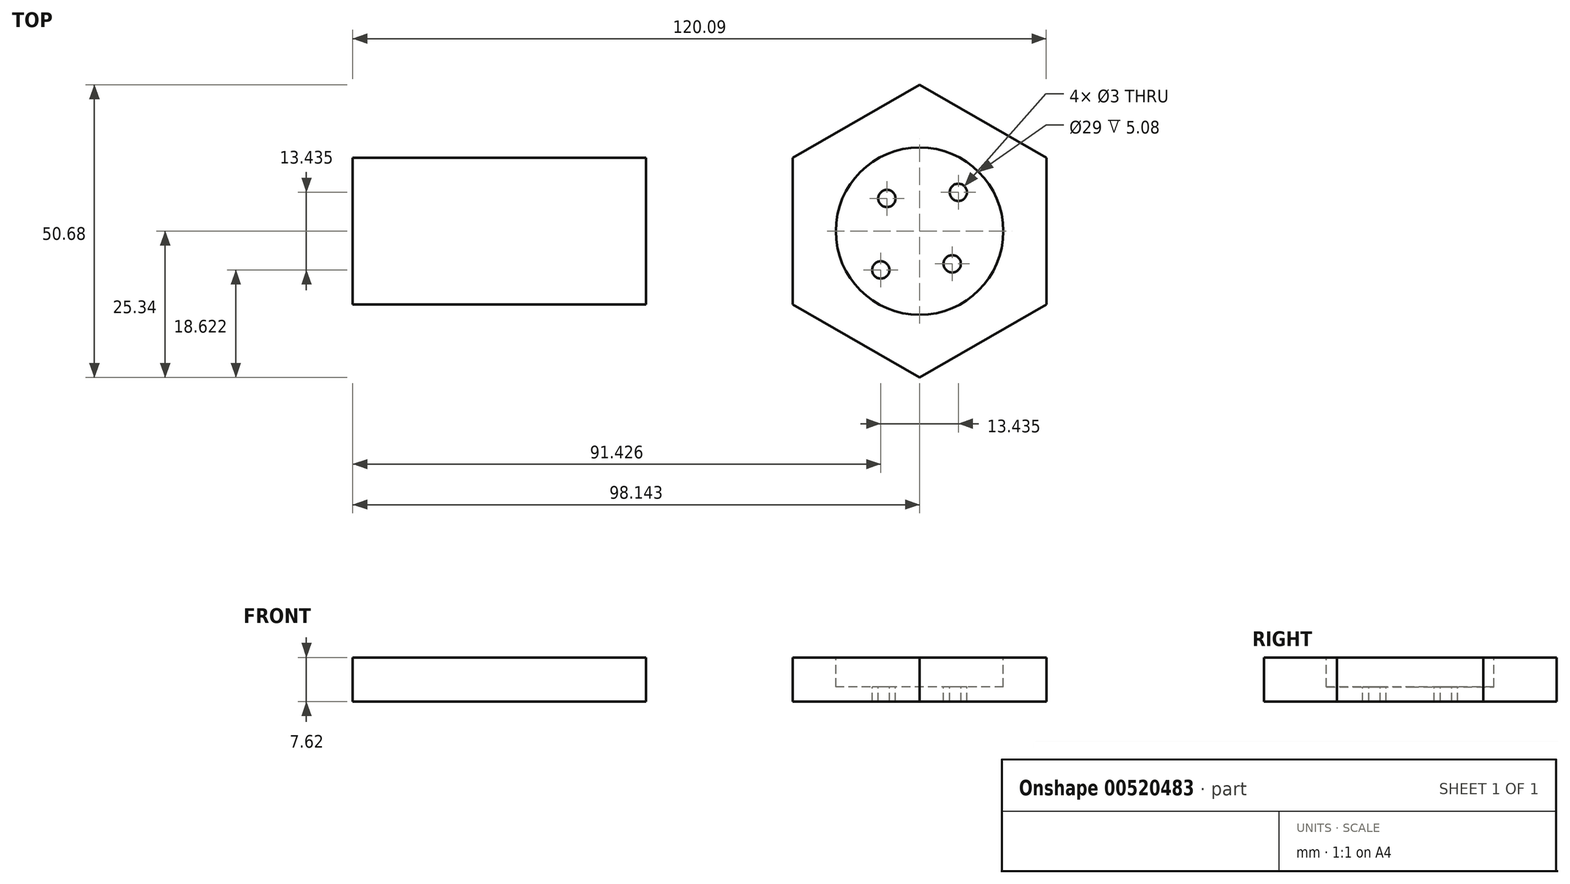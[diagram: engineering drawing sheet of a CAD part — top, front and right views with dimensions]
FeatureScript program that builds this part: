
annotation { "Feature Type Name" : "Feature", "Feature Type Description" : "" }
export const myFeature = defineFeature(function(context is Context, id is Id, definition is map)
    precondition{}
    {
        {
            var Q0;
            Q0=qCreatedBy(makeId("Top.planeOp"),FACE);
            var sketch = newSketch(context, id + "F0", { "sketchPlane" : qUnion([Q0])});
            skLineSegment(sketch, "E0.bottom", {"start": v(25.4, -12.7) * mm, "end": v(-25.4, -12.7) * mm});
            skLineSegment(sketch, "E0.top", {"start": v(25.4, 12.7) * mm, "end": v(-25.4, 12.7) * mm});
            skLineSegment(sketch, "E0.left", {"start": v(25.4, -12.7) * mm, "end": v(25.4, 12.7) * mm});
            skLineSegment(sketch, "E0.right", {"start": v(-25.4, -12.7) * mm, "end": v(-25.4, 12.7) * mm});
            skPoint(sketch, "E0.middle", {"position": v(0, 0) * mm});
            skSolve(sketch);
        }
        {
            var Q0;
            Q0=qCreatedBy(makeId("Top.planeOp"),FACE);
            var sketch = newSketch(context, id + "F1", { "sketchPlane" : qUnion([Q0])});
            skCircle(sketch, "E1.cCircle", {"center": v(72.74, 0) * mm, "radius": 21.95 * mm, "construction": true});
            skLineSegment(sketch, "E1.0", {"start": v(94.7, 12.67) * mm, "end": v(94.7, -12.67) * mm});
            skLineSegment(sketch, "E1.1", {"start": v(94.7, -12.67) * mm, "end": v(72.74, -25.34) * mm});
            skLineSegment(sketch, "E1.2", {"start": v(72.74, -25.34) * mm, "end": v(50.8, -12.67) * mm});
            skLineSegment(sketch, "E1.3", {"start": v(50.8, -12.67) * mm, "end": v(50.8, 12.67) * mm});
            skLineSegment(sketch, "E1.4", {"start": v(50.8, 12.67) * mm, "end": v(72.74, 25.34) * mm});
            skLineSegment(sketch, "E1.5", {"start": v(72.74, 25.34) * mm, "end": v(94.7, 12.67) * mm});
            skPoint(sketch, "E1.0.midPoint", {"position": v(94.7, 0) * mm});
            skSolve(sketch);
        }
        {
            var Q0;
            Q0=makeQuery(id+"F1.imprint","IMPRINT",FACE,{"disambiguationData":[TD([[makeQuery(id+"F1.imprint","IMPRINT",EDGE,{"derivedFrom":sQuery(id+"F1.wireOp",EDGE,"E1.0")}),-1.0]])]});
            extrude(context, id + "F2", {"entities" : qUnion([Q0]), "depth" : 7.62 * mm, "offsetDistance" : 25.4 * mm});
        }
        {
            var Q0;
            Q0=makeQuery(id+"F2.opExtrude","CAP_FACE",FACE,{"disambiguationData":[OSD([sQuery(id+"F1.wireOp",EDGE,"E1.0"),sQuery(id+"F1.wireOp",EDGE,"E1.1"),sQuery(id+"F1.wireOp",EDGE,"E1.2"),sQuery(id+"F1.wireOp",EDGE,"E1.3"),sQuery(id+"F1.wireOp",EDGE,"E1.4"),sQuery(id+"F1.wireOp",EDGE,"E1.5")])],"isStart":false});
            var sketch = newSketch(context, id + "F3", { "sketchPlane" : qUnion([Q0])});
            skCircle(sketch, "E2", {"center": v(72.74, 0) * mm, "radius": 14.5 * mm});
            skSolve(sketch);
        }
        {
            var Q0;
            Q0 = qSketchRegion(id + "F3", true);
            extrude(context, id + "F4", {"entities" : qUnion([Q0]), "operationType" : NewBodyOperationType.REMOVE, "oppositeDirection" : true, "depth" : 5.08 * mm, "offsetDistance" : 25.4 * mm});
        }
        {
            var Q0;
            Q0=makeQuery(id+"F4.boolean.opBoolean","COPY",FACE,{"derivedFrom":makeQuery(id+"F4.opExtrude","CAP_FACE",FACE,{"disambiguationData":[OSD([sQuery(id+"F3.wireOp",EDGE,"E2")])],"isStart":false})});
            var sketch = newSketch(context, id + "F5", { "sketchPlane" : qUnion([Q0])});
            skLineSegment(sketch, "E3", {"start": v(72.74, 0) * mm, "end": v(79.46, 6.72) * mm});
            skSolve(sketch);
        }
        {
            var Q0;
            Q0=makeQuery(id+"F5.imprint","IMPRINT",FACE,{"disambiguationData":[TD([[makeQuery(id+"F5.imprint","IMPRINT",EDGE,{"derivedFrom":makeQuery(id+"F4.boolean.opBoolean","COPY",EDGE,{"derivedFrom":makeQuery(id+"F4.opExtrude","CAP_EDGE",EDGE,{"disambiguationData":[OSD([sQuery(id+"F3.wireOp",EDGE,"E2")])],"isStart":false})})}),1.0]])]});
            var sketch = newSketch(context, id + "F6", { "sketchPlane" : qUnion([Q0])});
            skCircle(sketch, "E4", {"center": v(67.09, 5.66) * mm, "radius": 1.5 * mm});
            skSolve(sketch);
        }
        {
            var Q0;
            Q0=makeQuery(id+"F5.imprint","IMPRINT",FACE,{"disambiguationData":[TD([[makeQuery(id+"F5.imprint","IMPRINT",EDGE,{"derivedFrom":makeQuery(id+"F4.boolean.opBoolean","COPY",EDGE,{"derivedFrom":makeQuery(id+"F4.opExtrude","CAP_EDGE",EDGE,{"disambiguationData":[OSD([sQuery(id+"F3.wireOp",EDGE,"E2")])],"isStart":false})})}),1.0]])]});
            var sketch = newSketch(context, id + "F7", { "sketchPlane" : qUnion([Q0])});
            skCircle(sketch, "E5", {"center": v(79.46, 6.72) * mm, "radius": 1.5 * mm});
            skSolve(sketch);
        }
        {
            var Q0;
            Q0=makeQuery(id+"F5.imprint","IMPRINT",FACE,{"disambiguationData":[TD([[makeQuery(id+"F5.imprint","IMPRINT",EDGE,{"derivedFrom":makeQuery(id+"F4.boolean.opBoolean","COPY",EDGE,{"derivedFrom":makeQuery(id+"F4.opExtrude","CAP_EDGE",EDGE,{"disambiguationData":[OSD([sQuery(id+"F3.wireOp",EDGE,"E2")])],"isStart":false})})}),1.0]])]});
            var sketch = newSketch(context, id + "F8", { "sketchPlane" : qUnion([Q0])});
            skCircle(sketch, "E6", {"center": v(78.4, -5.66) * mm, "radius": 1.5 * mm});
            skSolve(sketch);
        }
        {
            var Q0;
            Q0=makeQuery(id+"F5.imprint","IMPRINT",FACE,{"disambiguationData":[TD([[makeQuery(id+"F5.imprint","IMPRINT",EDGE,{"derivedFrom":makeQuery(id+"F4.boolean.opBoolean","COPY",EDGE,{"derivedFrom":makeQuery(id+"F4.opExtrude","CAP_EDGE",EDGE,{"disambiguationData":[OSD([sQuery(id+"F3.wireOp",EDGE,"E2")])],"isStart":false})})}),1.0]])]});
            var sketch = newSketch(context, id + "F9", { "sketchPlane" : qUnion([Q0])});
            skCircle(sketch, "E7", {"center": v(66.03, -6.72) * mm, "radius": 1.5 * mm});
            skSolve(sketch);
        }
        {
            var Q0;
            Q0 = qSketchRegion(id + "F6", true);
            extrude(context, id + "F10", {"entities" : qUnion([Q0]), "operationType" : NewBodyOperationType.REMOVE, "endBound" : BoundingType.THROUGH_ALL, "oppositeDirection" : true, "depth" : 25.4 * mm, "offsetDistance" : 25.4 * mm});
        }
        {
            var Q0;
            Q0 = qSketchRegion(id + "F7", true);
            extrude(context, id + "F11", {"entities" : qUnion([Q0]), "operationType" : NewBodyOperationType.REMOVE, "endBound" : BoundingType.THROUGH_ALL, "oppositeDirection" : true, "depth" : 25.4 * mm, "offsetDistance" : 25.4 * mm});
        }
        {
            var Q0;
            Q0 = qSketchRegion(id + "F8", true);
            extrude(context, id + "F12", {"entities" : qUnion([Q0]), "operationType" : NewBodyOperationType.REMOVE, "endBound" : BoundingType.THROUGH_ALL, "oppositeDirection" : true, "depth" : 25.4 * mm, "offsetDistance" : 25.4 * mm});
        }
        {
            var Q0;
            Q0 = qSketchRegion(id + "F9", true);
            extrude(context, id + "F13", {"entities" : qUnion([Q0]), "operationType" : NewBodyOperationType.REMOVE, "endBound" : BoundingType.THROUGH_ALL, "oppositeDirection" : true, "depth" : 25.4 * mm, "offsetDistance" : 25.4 * mm});
        }
        {
            var Q0;
            Q0 = qSketchRegion(id + "F0", true);
            extrude(context, id + "F14", {"entities" : qUnion([Q0]), "depth" : 7.62 * mm, "offsetDistance" : 25.4 * mm});
        }
    });
